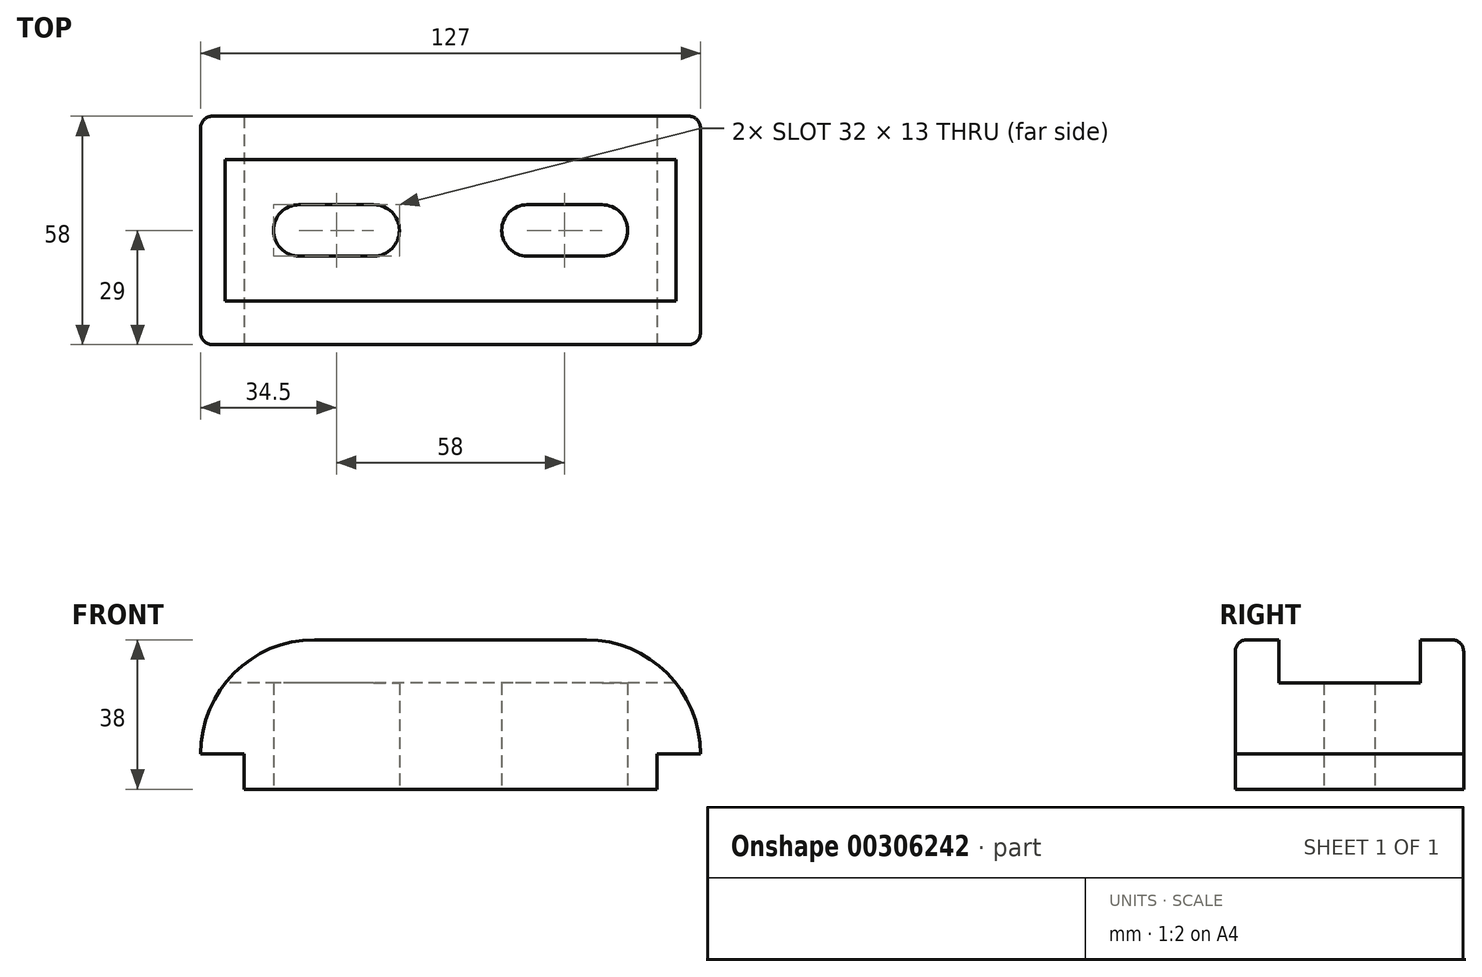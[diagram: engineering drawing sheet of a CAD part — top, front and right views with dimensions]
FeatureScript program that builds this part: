
annotation { "Feature Type Name" : "Feature", "Feature Type Description" : "" }
export const myFeature = defineFeature(function(context is Context, id is Id, definition is map)
    precondition{}
    {
        {
            var Q0;
            Q0=qCreatedBy(makeId("Front.planeOp"),FACE);
            var sketch = newSketch(context, id + "F0", { "sketchPlane" : qUnion([Q0])});
            skLineSegment(sketch, "E0", {"start": v(11, 0) * mm, "end": v(116, 0) * mm});
            skLineSegment(sketch, "E1", {"start": v(116, 0) * mm, "end": v(116, 9) * mm});
            skLineSegment(sketch, "E2", {"start": v(116, 9) * mm, "end": v(127, 9) * mm});
            skLineSegment(sketch, "E3", {"start": v(11, 9) * mm, "end": v(0, 9) * mm});
            skLineSegment(sketch, "E4", {"start": v(11, 0) * mm, "end": v(11, 9) * mm});
            skLineSegment(sketch, "E5", {"start": v(29, 38) * mm, "end": v(98, 38) * mm});
            skArc(sketch, "E6", {"start": v(29, 38) * mm, "mid": v(8.5, 29.5) * mm, "end": v(0, 9) * mm});
            skArc(sketch, "E7", {"start": v(127, 9) * mm, "mid": v(118.5, 29.5) * mm, "end": v(98, 38) * mm});
            skSolve(sketch);
        }
        {
            var Q0;
            Q0 = qSketchRegion(id + "F0", true);
            extrude(context, id + "F1", {"entities" : qUnion([Q0]), "endBound" : BoundingType.SYMMETRIC, "oppositeDirection" : true, "depth" : 58 * mm});
        }
        {
            var Q0;
            Q0=makeQuery(id+"F1.opExtrude","CAP_EDGE",EDGE,{"disambiguationData":[OSD([sQuery(id+"F0.wireOp",EDGE,"E5")])],"isStart":true});
            var Q1;
            Q1=makeQuery(id+"F1.opExtrude","CAP_EDGE",EDGE,{"disambiguationData":[OSD([sQuery(id+"F0.wireOp",EDGE,"E5")])],"isStart":false});
            fillet(context, id + "F2", {"entities" : qUnion([Q0, Q1]), "radius" : 3 * mm, "tangentPropagation" : true, "allowEdgeOverflow" : false});
        }
        {
            var Q0;
            Q0=qCreatedBy(makeId("Right.planeOp"),FACE);
            var sketch = newSketch(context, id + "F3", { "sketchPlane" : qUnion([Q0])});
            skLineSegment(sketch, "E8.bottom", {"start": v(-18, 38) * mm, "end": v(18, 38) * mm});
            skLineSegment(sketch, "E8.top", {"start": v(-18, 27) * mm, "end": v(18, 27) * mm});
            skLineSegment(sketch, "E8.left", {"start": v(-18, 38) * mm, "end": v(-18, 27) * mm});
            skLineSegment(sketch, "E8.right", {"start": v(18, 38) * mm, "end": v(18, 27) * mm});
            skSolve(sketch);
        }
        {
            var Q0;
            Q0 = qSketchRegion(id + "F3", true);
            extrude(context, id + "F4", {"entities" : qUnion([Q0]), "operationType" : NewBodyOperationType.REMOVE, "endBound" : BoundingType.THROUGH_ALL, "depth" : 25 * mm});
        }
        {
            var Q0;
            Q0=qCreatedBy(makeId("Top.planeOp"),FACE);
            var sketch = newSketch(context, id + "F5", { "sketchPlane" : qUnion([Q0])});
            skLineSegment(sketch, "E9", {"start": v(25, 6.5) * mm, "end": v(44, 6.5) * mm});
            skLineSegment(sketch, "E10", {"start": v(25, -6.5) * mm, "end": v(44, -6.5) * mm});
            skLineSegment(sketch, "E11", {"start": v(83, 6.5) * mm, "end": v(102, 6.5) * mm});
            skLineSegment(sketch, "E12", {"start": v(83, -6.5) * mm, "end": v(102, -6.5) * mm});
            skArc(sketch, "E13", {"start": v(25, 6.5) * mm, "mid": v(18.5, 0) * mm, "end": v(25, -6.5) * mm});
            skArc(sketch, "E14", {"start": v(44, -6.5) * mm, "mid": v(50.5, 0) * mm, "end": v(44, 6.5) * mm});
            skArc(sketch, "E15", {"start": v(83, 6.5) * mm, "mid": v(76.5, 0) * mm, "end": v(83, -6.5) * mm});
            skArc(sketch, "E16", {"start": v(102, -6.5) * mm, "mid": v(108.5, 0) * mm, "end": v(102, 6.5) * mm});
            skSolve(sketch);
        }
        {
            var Q0;
            Q0 = qSketchRegion(id + "F5", true);
            extrude(context, id + "F6", {"entities" : qUnion([Q0]), "operationType" : NewBodyOperationType.REMOVE, "endBound" : BoundingType.THROUGH_ALL, "depth" : 25 * mm});
        }
    });
